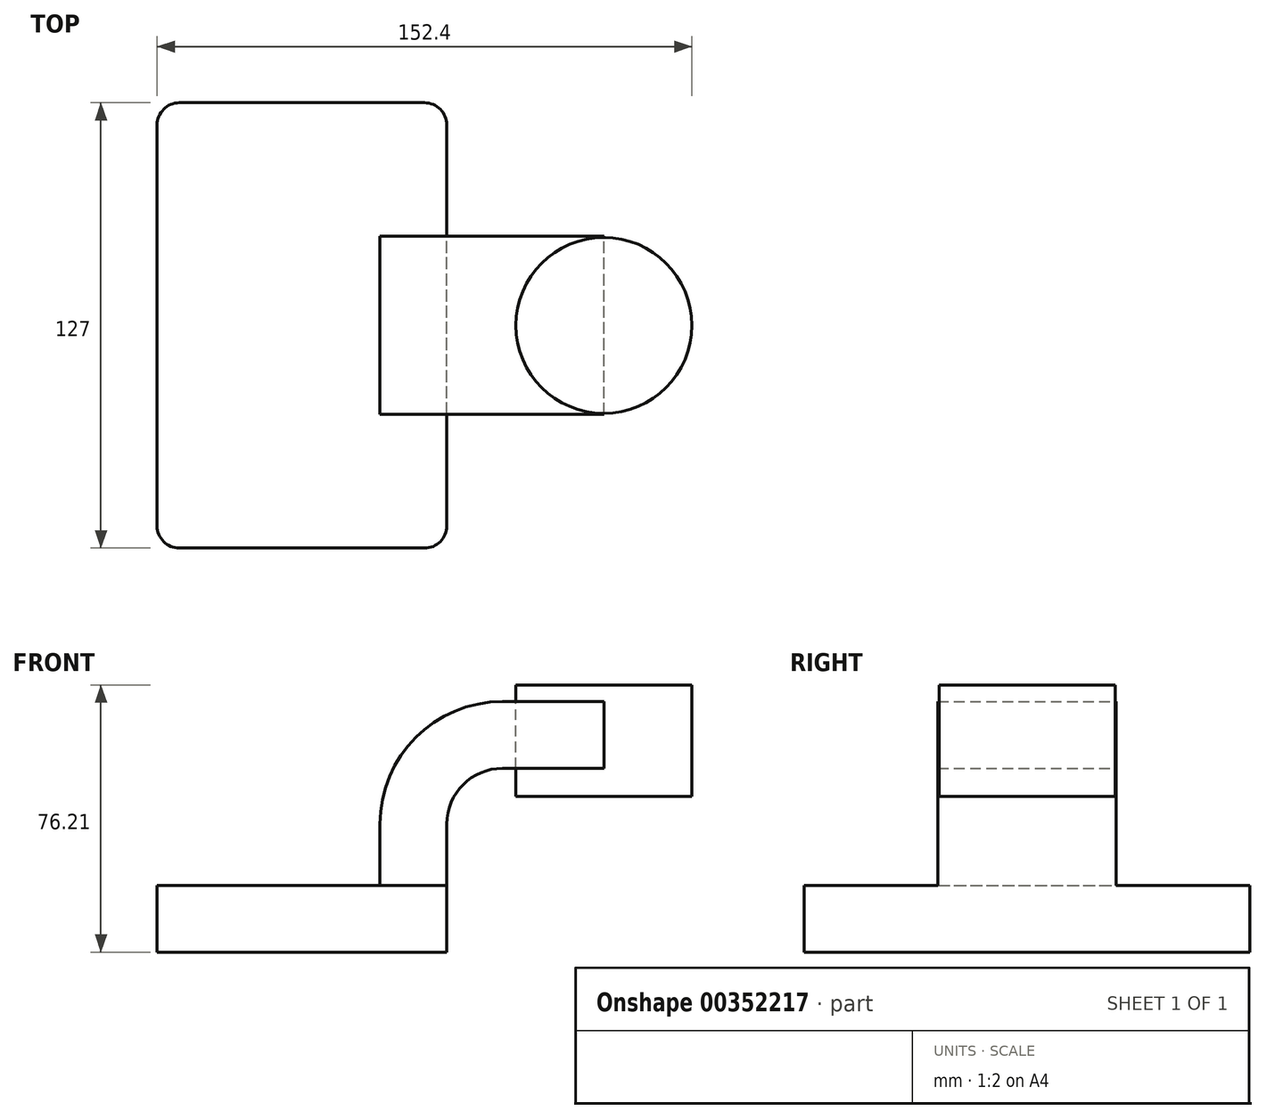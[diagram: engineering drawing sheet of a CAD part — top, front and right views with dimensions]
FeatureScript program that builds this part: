
annotation { "Feature Type Name" : "Feature", "Feature Type Description" : "" }
export const myFeature = defineFeature(function(context is Context, id is Id, definition is map)
    precondition{}
    {
        {
            var Q0;
            Q0=qCreatedBy(makeId("Front.planeOp"),FACE);
            var sketch = newSketch(context, id + "F0", { "sketchPlane" : qUnion([Q0])});
            skLineSegment(sketch, "E0.bottom", {"start": v(-41.28, 9.52) * mm, "end": v(41.28, 9.53) * mm});
            skLineSegment(sketch, "E0.top", {"start": v(-41.28, -9.53) * mm, "end": v(41.28, -9.53) * mm});
            skLineSegment(sketch, "E0.left", {"start": v(-41.28, 9.52) * mm, "end": v(-41.27, -9.53) * mm});
            skLineSegment(sketch, "E0.right", {"start": v(41.28, 9.53) * mm, "end": v(41.28, -9.52) * mm});
            skPoint(sketch, "E0.middle", {"position": v(0, 0) * mm});
            skLineSegment(sketch, "E1.bottom", {"start": v(60.33, 66.68) * mm, "end": v(111.13, 66.68) * mm});
            skLineSegment(sketch, "E1.top", {"start": v(60.33, 34.93) * mm, "end": v(111.13, 34.93) * mm});
            skLineSegment(sketch, "E1.left", {"start": v(60.33, 66.67) * mm, "end": v(60.33, 34.92) * mm});
            skLineSegment(sketch, "E1.right", {"start": v(111.13, 66.68) * mm, "end": v(111.13, 34.93) * mm});
            skPoint(sketch, "E1.middle", {"position": v(85.73, 50.8) * mm});
            skLineSegment(sketch, "E2", {"start": v(41.27, 9.53) * mm, "end": v(41.27, 27) * mm});
            skArc(sketch, "E3", {"start": v(41.27, 27) * mm, "mid": v(45.92, 38.23) * mm, "end": v(57.15, 42.88) * mm});
            skLineSegment(sketch, "E4", {"start": v(57.15, 42.88) * mm, "end": v(86.04, 42.88) * mm});
            skLineSegment(sketch, "E5.0", {"start": v(57.15, 61.93) * mm, "end": v(86.04, 61.93) * mm});
            skArc(sketch, "E5.1", {"start": v(22.22, 27) * mm, "mid": v(32.45, 51.7) * mm, "end": v(57.15, 61.93) * mm});
            skLineSegment(sketch, "E5.2", {"start": v(22.22, 9.53) * mm, "end": v(22.22, 27) * mm});
            skLineSegment(sketch, "E6", {"start": v(86.04, 61.93) * mm, "end": v(86.04, 42.88) * mm});
            skFitSpline(sketch, "E7", {"points": [v(-41.28, 9.53) * mm, v(57.15, 61.93) * mm], "startDerivative": vector(-1.22, 97.24) * mm, "endDerivative": vector(147.32, -3.38) * mm});
            skLineSegment(sketch, "E8", {"start": v(86.04, 66.68) * mm, "end": v(86.04, 34.93) * mm});
            skSolve(sketch);
        }
        {
            var Q0;
            Q0=makeQuery(id+"F0.imprint","IMPRINT",FACE,{"disambiguationData":[TD([[makeQuery(id+"F0.imprint","IMPRINT",EDGE,{"derivedFrom":sQuery(id+"F0.wireOp",EDGE,"E0.top")}),1.0]])]});
            extrude(context, id + "F1", {"entities" : qUnion([Q0]), "endBound" : BoundingType.SYMMETRIC, "depth" : 127 * mm});
        }
        {
            var Q0;
            {var subQ1=sQuery(id+"F0.wireOp",EDGE,"E2");Q0=makeQuery(id+"F0.imprint","IMPRINT",FACE,{"disambiguationData":[TD([[makeQuery(id+"F0.imprint","IMPRINT",EDGE,{"derivedFrom":subQ1}),1.0]])]});}
            var Q1;
            {var subQ0=sQuery(id+"F0.wireOp",EDGE,"E5.0");var subQ1=sQuery(id+"F0.wireOp",EDGE,"E1.left");var subQ2=makeQuery(id+"F0.imprint","INTERSECT",VERTEX,{"derivedFrom":[subQ1,subQ0]});Q1=makeQuery(id+"F0.imprint","IMPRINT",FACE,{"disambiguationData":[TD([[makeQuery(id+"F0.imprint","IMPRINT",EDGE,{"disambiguationData":[TD([[subQ2,-1.0]])],"derivedFrom":subQ1}),1.0]])]});}
            extrude(context, id + "F2", {"entities" : qUnion([Q0, Q1]), "operationType" : NewBodyOperationType.ADD, "endBound" : BoundingType.SYMMETRIC, "depth" : 50.8 * mm});
        }
        {
            var Q0;
            Q0=makeQuery(id+"F0.imprint","IMPRINT",FACE,{"disambiguationData":[TD([[makeQuery(id+"F0.imprint","IMPRINT",EDGE,{"derivedFrom":sQuery(id+"F0.wireOp",EDGE,"E5.1")}),1.0]])]});
            extrude(context, id + "F3", {"entities" : qUnion([Q0]), "operationType" : NewBodyOperationType.ADD, "endBound" : BoundingType.SYMMETRIC, "depth" : 13.97 * mm});
        }
        {
            var Q0;
            {var subQ4=sQuery(id+"F0.wireOp",EDGE,"E1.right");Q0=makeQuery(id+"F0.imprint","IMPRINT",FACE,{"disambiguationData":[TD([[makeQuery(id+"F0.imprint","IMPRINT",EDGE,{"derivedFrom":subQ4}),-1.0]])]});}
            var Q1;
            Q1=sQuery(id+"F0.wireOp",EDGE,"E8");
            revolve(context, id + "F4", {"entities" : qUnion([Q0]), "axis" : qUnion([Q1]), "revolveType" : RevolveType.FULL});
        }
        {
            var Q0;
            Q0=makeQuery(id+"F1.opExtrude","CAP_EDGE",EDGE,{"disambiguationData":[OSD([sQuery(id+"F0.wireOp",EDGE,"E0.left")])],"isStart":false});
            var Q1;
            Q1=makeQuery(id+"F1.opExtrude","CAP_EDGE",EDGE,{"disambiguationData":[OSD([sQuery(id+"F0.wireOp",EDGE,"E0.right")])],"isStart":false});
            var Q2;
            Q2=makeQuery(id+"F1.opExtrude","CAP_EDGE",EDGE,{"disambiguationData":[OSD([sQuery(id+"F0.wireOp",EDGE,"E0.right")])],"isStart":true});
            var Q3;
            Q3=makeQuery(id+"F1.opExtrude","CAP_EDGE",EDGE,{"disambiguationData":[OSD([sQuery(id+"F0.wireOp",EDGE,"E0.left")])],"isStart":true});
            fillet(context, id + "F5", {"entities" : qUnion([Q0, Q1, Q2, Q3]), "radius" : 6.35 * mm, "tangentPropagation" : true, "allowEdgeOverflow" : false});
        }
    });
